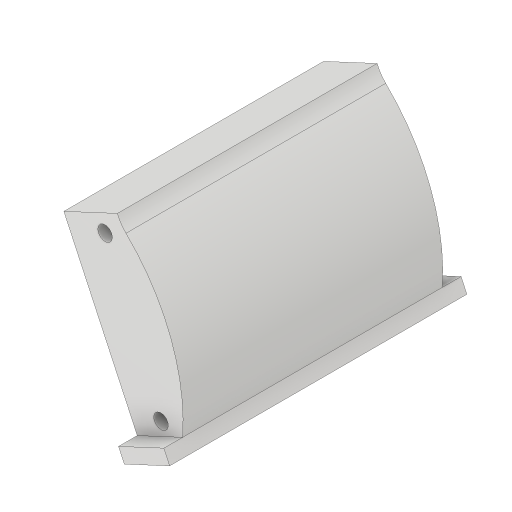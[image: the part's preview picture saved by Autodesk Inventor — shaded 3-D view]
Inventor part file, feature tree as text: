
AUTODESK INVENTOR PART (.ipt)
format: ipt  version: 2023.2 (Build 272271000, 271)  size: 194,048 bytes
history: native  units: mm
features: extrude x5, sketch x5, projected_geometry x3, other x1
ambient origin geometry x8: Origin, YZ Plane, XZ Plane, XY Plane, X Axis, Y Axis, Z Axis, Center Point
bodies: Body1 (feature_tree)
feature tree (14):
  other  "솔리드1"
  extrude  "돌출1"  Depth=5.0mm TaperAngle=90.0deg
  extrude  "돌출2"  Depth=56.8mm TaperAngle=0.0deg
  extrude  "돌출3"  Depth=5.0mm TaperAngle=90.0deg
  extrude  "돌출4"  Depth=57.0mm TaperAngle=0.0deg
  extrude  "돌출7"  Depth=65.0mm
  sketch  "스케치1"
  sketch  "스케치2"
  sketch  "스케치3"
  sketch  "스케치4"
  projected_geometry  "투영된 루프1"
  projected_geometry  "투영된 루프2"
  sketch  "스케치8"
  projected_geometry  "투영된 루프4"
